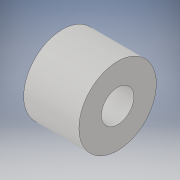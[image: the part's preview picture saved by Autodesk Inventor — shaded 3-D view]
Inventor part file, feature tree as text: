
AUTODESK INVENTOR PART (.ipt)
format: ipt  version: 2019 (Build 230136000, 136)  size: 94,720 bytes
history: native  units: mm
features: extrude x1, sketch x1
ambient origin geometry x8: Origin, YZ Plane, XZ Plane, XY Plane, X Axis, Y Axis, Z Axis, Center Point
bodies: Solid1 (feature_tree)
feature tree (2):
  extrude  "Extrusion1"  Depth=25.0mm TaperAngle=0.0deg
  sketch  "Sketch1"  dims[d0=35.0mm d1=25.0mm d2=0.0mm]
